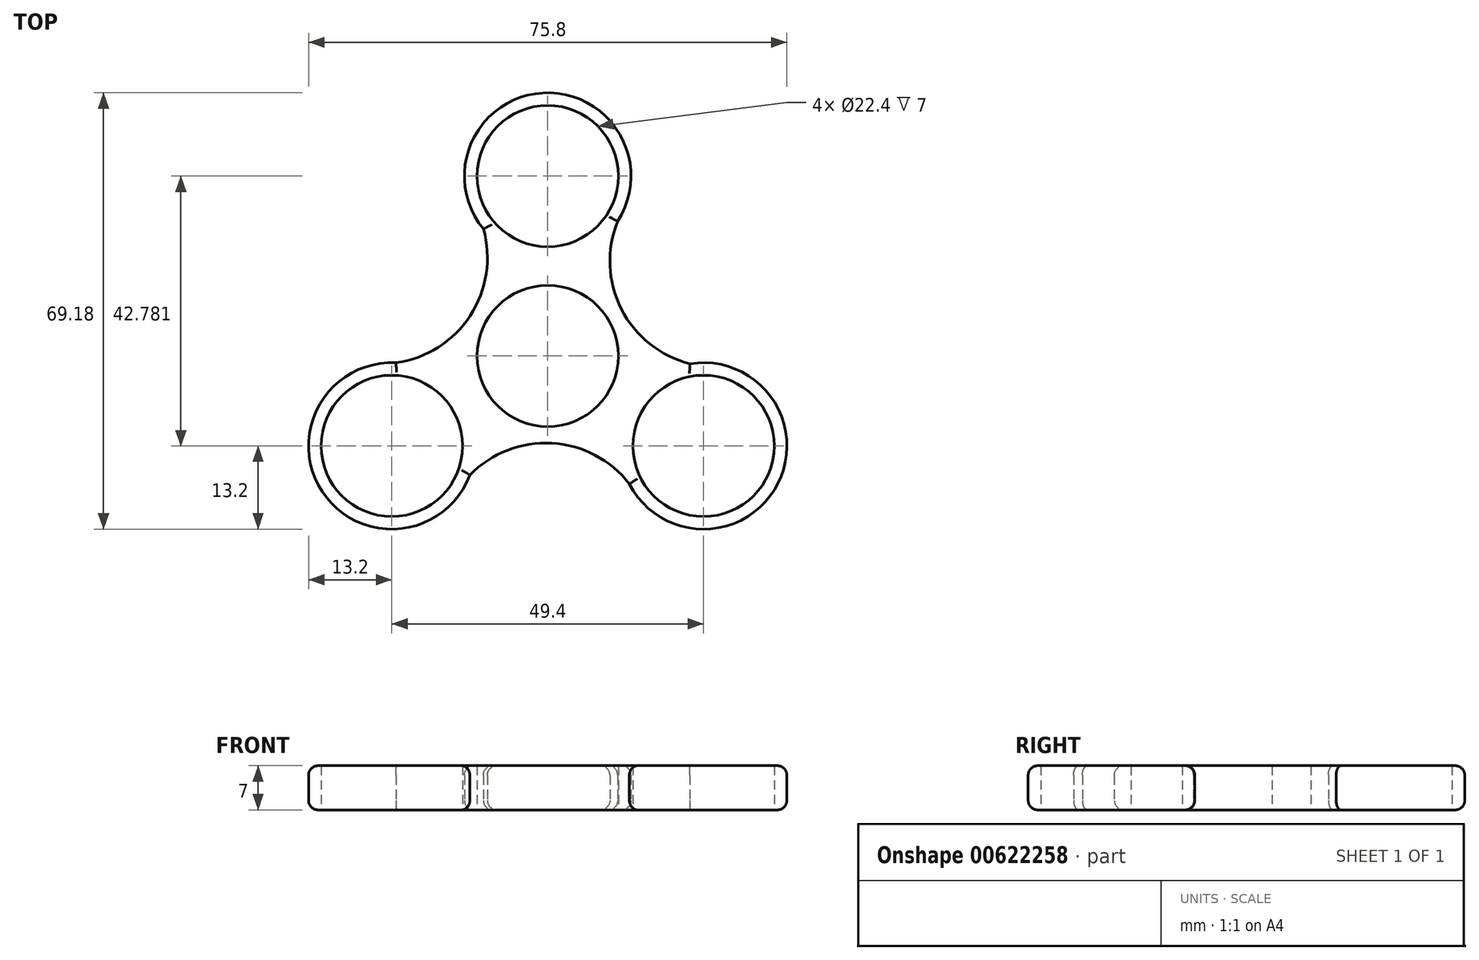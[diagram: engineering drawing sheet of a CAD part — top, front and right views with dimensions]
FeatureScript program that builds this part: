
annotation { "Feature Type Name" : "Feature", "Feature Type Description" : "" }
export const myFeature = defineFeature(function(context is Context, id is Id, definition is map)
    precondition{}
    {
        {
            var Q0;
            Q0=qCreatedBy(makeId("Top.planeOp"),FACE);
            var sketch = newSketch(context, id + "F0", { "sketchPlane" : qUnion([Q0])});
            skCircle(sketch, "E0", {"center": v(0, 0) * mm, "radius": 11.2 * mm});
            skCircle(sketch, "E1", {"center": v(0, 28.52) * mm, "radius": 11.2 * mm});
            skArc(sketch, "E2", {"start": v(11.08, 21.35) * mm, "mid": v(-0.76, 41.7) * mm, "end": v(-10.18, 20.12) * mm});
            skCircle(sketch, "E3.1.0", {"center": v(-24.7, -14.26) * mm, "radius": 11.2 * mm});
            skArc(sketch, "E3.1.1", {"start": v(-24.03, -1.08) * mm, "mid": v(-35.73, -21.5) * mm, "end": v(-12.34, -18.88) * mm});
            skCircle(sketch, "E3.2.0", {"center": v(24.7, -14.26) * mm, "radius": 11.2 * mm});
            skArc(sketch, "E3.2.1", {"start": v(12.95, -20.27) * mm, "mid": v(36.5, -20.2) * mm, "end": v(22.52, -1.24) * mm});
            skArc(sketch, "E4", {"start": v(11.08, 21.35) * mm, "mid": v(11.67, 7.45) * mm, "end": v(22.52, -1.24) * mm});
            skArc(sketch, "E5.1.0", {"start": v(-24.03, -1.08) * mm, "mid": v(-12.29, 6.38) * mm, "end": v(-10.18, 20.12) * mm});
            skArc(sketch, "E5.2.0", {"start": v(12.95, -20.27) * mm, "mid": v(0.62, -13.83) * mm, "end": v(-12.34, -18.88) * mm});
            skSolve(sketch);
        }
        {
            var Q0;
            Q0=makeQuery(id+"F0.imprint","IMPRINT",FACE,{"disambiguationData":[TD([[makeQuery(id+"F0.imprint","IMPRINT",EDGE,{"derivedFrom":sQuery(id+"F0.wireOp",EDGE,"E0")}),-1.0]])]});
            extrude(context, id + "F1", {"entities" : qUnion([Q0]), "depth" : 7 * mm, "offsetDistance" : 25 * mm});
        }
        {
            var Q0;
            Q0=makeQuery(id+"F1.opExtrude","CAP_EDGE",EDGE,{"disambiguationData":[OSD([sQuery(id+"F0.wireOp",EDGE,"E3.1.1")])],"isStart":false});
            var Q1;
            Q1=makeQuery(id+"F1.opExtrude","CAP_EDGE",EDGE,{"disambiguationData":[OSD([sQuery(id+"F0.wireOp",EDGE,"E5.1.0")])],"isStart":false});
            var Q2;
            Q2=makeQuery(id+"F1.opExtrude","CAP_EDGE",EDGE,{"disambiguationData":[OSD([sQuery(id+"F0.wireOp",EDGE,"E2")])],"isStart":false});
            var Q3;
            Q3=makeQuery(id+"F1.opExtrude","CAP_EDGE",EDGE,{"disambiguationData":[OSD([sQuery(id+"F0.wireOp",EDGE,"E4")])],"isStart":false});
            var Q4;
            Q4=makeQuery(id+"F1.opExtrude","CAP_EDGE",EDGE,{"disambiguationData":[OSD([sQuery(id+"F0.wireOp",EDGE,"E3.2.1")])],"isStart":false});
            var Q5;
            Q5=makeQuery(id+"F1.opExtrude","CAP_EDGE",EDGE,{"disambiguationData":[OSD([sQuery(id+"F0.wireOp",EDGE,"E5.2.0")])],"isStart":false});
            fillet(context, id + "F2", {"entities" : qUnion([Q0, Q1, Q2, Q3, Q4, Q5]), "radius" : 1.5 * mm, "tangentPropagation" : true, "allowEdgeOverflow" : false});
        }
        {
            var Q0;
            Q0=makeQuery(id+"F1.opExtrude","CAP_EDGE",EDGE,{"disambiguationData":[OSD([sQuery(id+"F0.wireOp",EDGE,"E3.2.1")])],"isStart":true});
            var Q1;
            Q1=makeQuery(id+"F1.opExtrude","CAP_EDGE",EDGE,{"disambiguationData":[OSD([sQuery(id+"F0.wireOp",EDGE,"E4")])],"isStart":true});
            var Q2;
            Q2=makeQuery(id+"F1.opExtrude","CAP_EDGE",EDGE,{"disambiguationData":[OSD([sQuery(id+"F0.wireOp",EDGE,"E2")])],"isStart":true});
            var Q3;
            Q3=makeQuery(id+"F1.opExtrude","CAP_EDGE",EDGE,{"disambiguationData":[OSD([sQuery(id+"F0.wireOp",EDGE,"E5.1.0")])],"isStart":true});
            var Q4;
            Q4=makeQuery(id+"F1.opExtrude","CAP_EDGE",EDGE,{"disambiguationData":[OSD([sQuery(id+"F0.wireOp",EDGE,"E3.1.1")])],"isStart":true});
            var Q5;
            Q5=makeQuery(id+"F1.opExtrude","CAP_EDGE",EDGE,{"disambiguationData":[OSD([sQuery(id+"F0.wireOp",EDGE,"E5.2.0")])],"isStart":true});
            fillet(context, id + "F3", {"entities" : qUnion([Q0, Q1, Q2, Q3, Q4, Q5]), "radius" : 1.5 * mm, "tangentPropagation" : true, "allowEdgeOverflow" : false});
        }
    });
